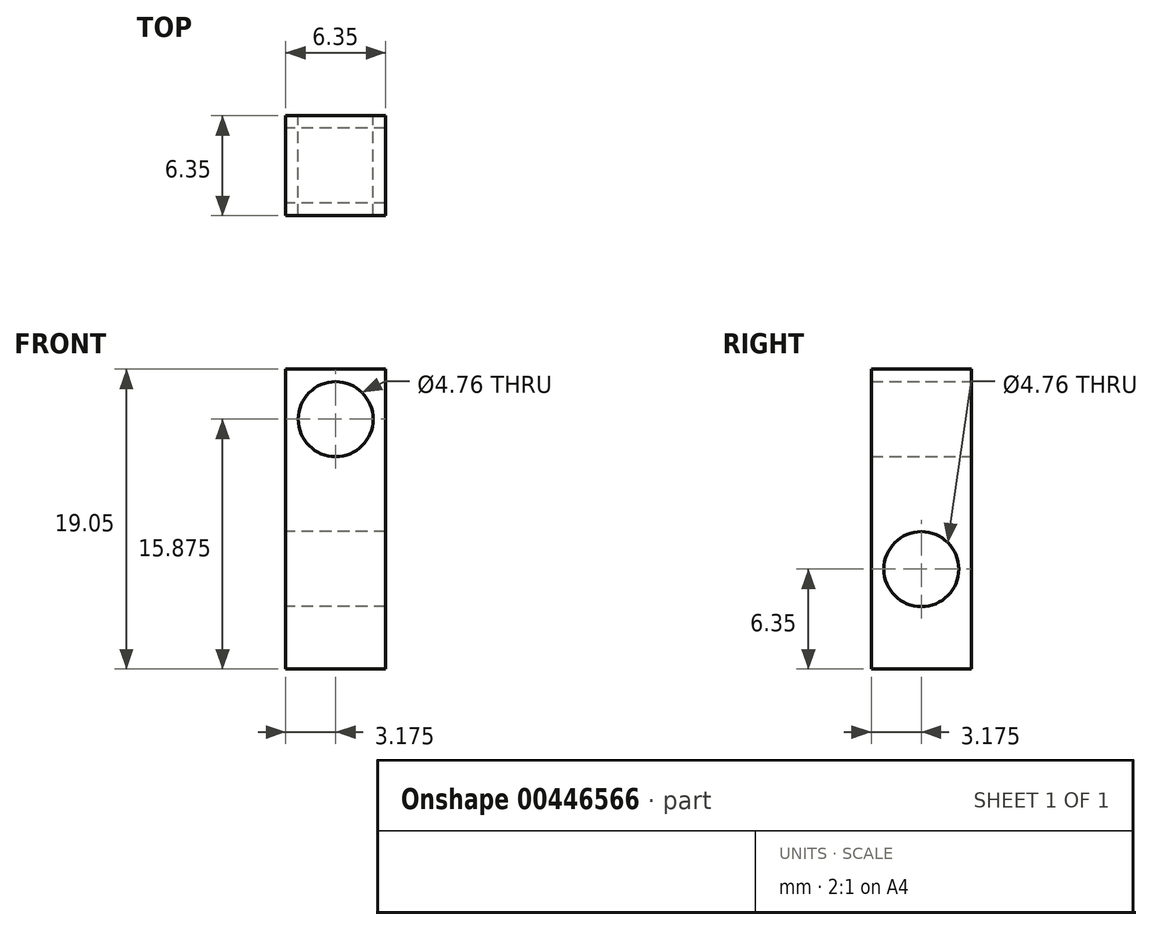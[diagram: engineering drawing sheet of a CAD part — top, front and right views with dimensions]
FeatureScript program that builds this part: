
annotation { "Feature Type Name" : "Feature", "Feature Type Description" : "" }
export const myFeature = defineFeature(function(context is Context, id is Id, definition is map)
    precondition{}
    {
        {
            var Q0;
            Q0=qCreatedBy(makeId("Right.planeOp"),FACE);
            var sketch = newSketch(context, id + "F0", { "sketchPlane" : qUnion([Q0])});
            skLineSegment(sketch, "E0.bottom", {"start": v(0, 0) * mm, "end": v(6.35, 0) * mm});
            skLineSegment(sketch, "E0.top", {"start": v(0, 19.05) * mm, "end": v(6.35, 19.05) * mm});
            skLineSegment(sketch, "E0.left", {"start": v(0, 0) * mm, "end": v(0, 19.05) * mm});
            skLineSegment(sketch, "E0.right", {"start": v(6.35, 0) * mm, "end": v(6.35, 19.05) * mm});
            skCircle(sketch, "E1", {"center": v(3.17, 6.35) * mm, "radius": 2.38 * mm});
            skPoint(sketch, "E2", {"position": v(3.18, 0) * mm});
            skSolve(sketch);
        }
        {
            var Q0;
            Q0 = qSketchRegion(id + "F0", true);
            extrude(context, id + "F1", {"entities" : qUnion([Q0]), "depth" : 6.35 * mm});
        }
        {
            var Q0;
            Q0=makeQuery(id+"F1.opExtrude","SWEPT_FACE",FACE,{"disambiguationData":[OSD([sQuery(id+"F0.wireOp",EDGE,"E0.right")])]});
            var sketch = newSketch(context, id + "F2", { "sketchPlane" : qUnion([Q0])});
            skCircle(sketch, "E3", {"center": v(-3.18, 15.88) * mm, "radius": 2.38 * mm});
            skPoint(sketch, "E3.centerSnap0", {"position": v(-3.18, 19.05) * mm});
            skSolve(sketch);
        }
        {
            var Q0;
            Q0 = qSketchRegion(id + "F2", true);
            extrude(context, id + "F3", {"entities" : qUnion([Q0]), "operationType" : NewBodyOperationType.REMOVE, "oppositeDirection" : true, "depth" : 25.4 * mm});
        }
    });
